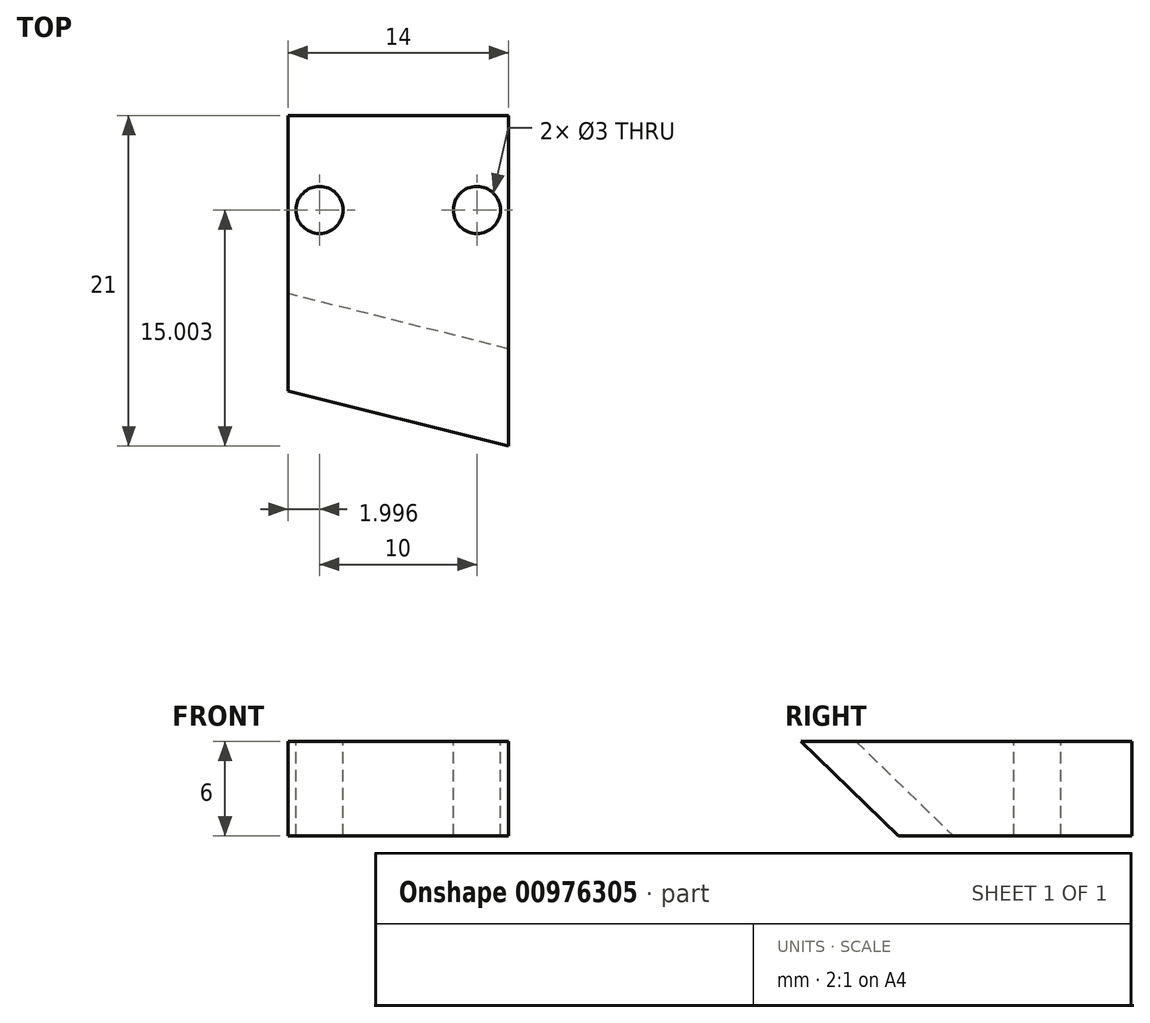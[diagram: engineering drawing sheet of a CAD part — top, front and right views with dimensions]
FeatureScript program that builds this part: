
annotation { "Feature Type Name" : "Feature", "Feature Type Description" : "" }
export const myFeature = defineFeature(function(context is Context, id is Id, definition is map)
    precondition{}
    {
        {
            var Q0;
            Q0=qCreatedBy(makeId("Top.planeOp"),FACE);
            var sketch = newSketch(context, id + "F0", { "sketchPlane" : qUnion([Q0])});
            skLineSegment(sketch, "E0.bottom", {"start": v(-3.73, 7.41) * mm, "end": v(10.27, 7.41) * mm});
            skLineSegment(sketch, "E0.top", {"start": v(-3.73, -13.59) * mm, "end": v(10.27, -13.59) * mm});
            skLineSegment(sketch, "E0.left", {"start": v(-3.73, 7.41) * mm, "end": v(-3.73, -13.59) * mm});
            skLineSegment(sketch, "E0.right", {"start": v(10.27, 7.41) * mm, "end": v(10.27, -13.59) * mm});
            skLineSegment(sketch, "E1", {"start": v(-3.73, -10.09) * mm, "end": v(10.27, -13.59) * mm});
            skSolve(sketch);
        }
        {
            var Q0;
            {var subQ0=sQuery(id+"F0.wireOp",EDGE,"E0.bottom");Q0=makeQuery(id+"F0.imprint","IMPRINT",FACE,{"disambiguationData":[TD([[makeQuery(id+"F0.imprint","IMPRINT",EDGE,{"derivedFrom":subQ0}),-1.0]])]});}
            extrude(context, id + "F1", {"entities" : qUnion([Q0]), "depth" : 6 * mm, "offsetDistance" : 25 * mm});
        }
        {
            var Q0;
            Q0=makeQuery(id+"F1.opExtrude","CAP_EDGE",EDGE,{"disambiguationData":[OSD([sQuery(id+"F0.wireOp",EDGE,"E1")])],"isStart":true});
            chamfer(context, id + "F2", {"entities" : qUnion([Q0]), "width" : 6 * mm, "tangentPropagation" : true});
        }
        {
            var Q0;
            Q0=makeQuery(id+"F1.opExtrude","CAP_FACE",FACE,{"disambiguationData":[OSD([sQuery(id+"F0.wireOp",EDGE,"E0.bottom"),sQuery(id+"F0.wireOp",EDGE,"E0.left"),sQuery(id+"F0.wireOp",EDGE,"E0.right"),sQuery(id+"F0.wireOp",EDGE,"E1")])],"isStart":false});
            var sketch = newSketch(context, id + "F3", { "sketchPlane" : qUnion([Q0])});
            skCircle(sketch, "E2", {"center": v(-1.73, 1.41) * mm, "radius": 1.5 * mm});
            skCircle(sketch, "E3", {"center": v(8.27, 1.41) * mm, "radius": 1.5 * mm});
            skSolve(sketch);
        }
        {
            var Q0;
            Q0 = qSketchRegion(id + "F3", true);
            extrude(context, id + "F4", {"entities" : qUnion([Q0]), "operationType" : NewBodyOperationType.REMOVE, "endBound" : BoundingType.UP_TO_NEXT, "oppositeDirection" : true, "depth" : 25 * mm, "offsetDistance" : 25 * mm});
        }
    });
